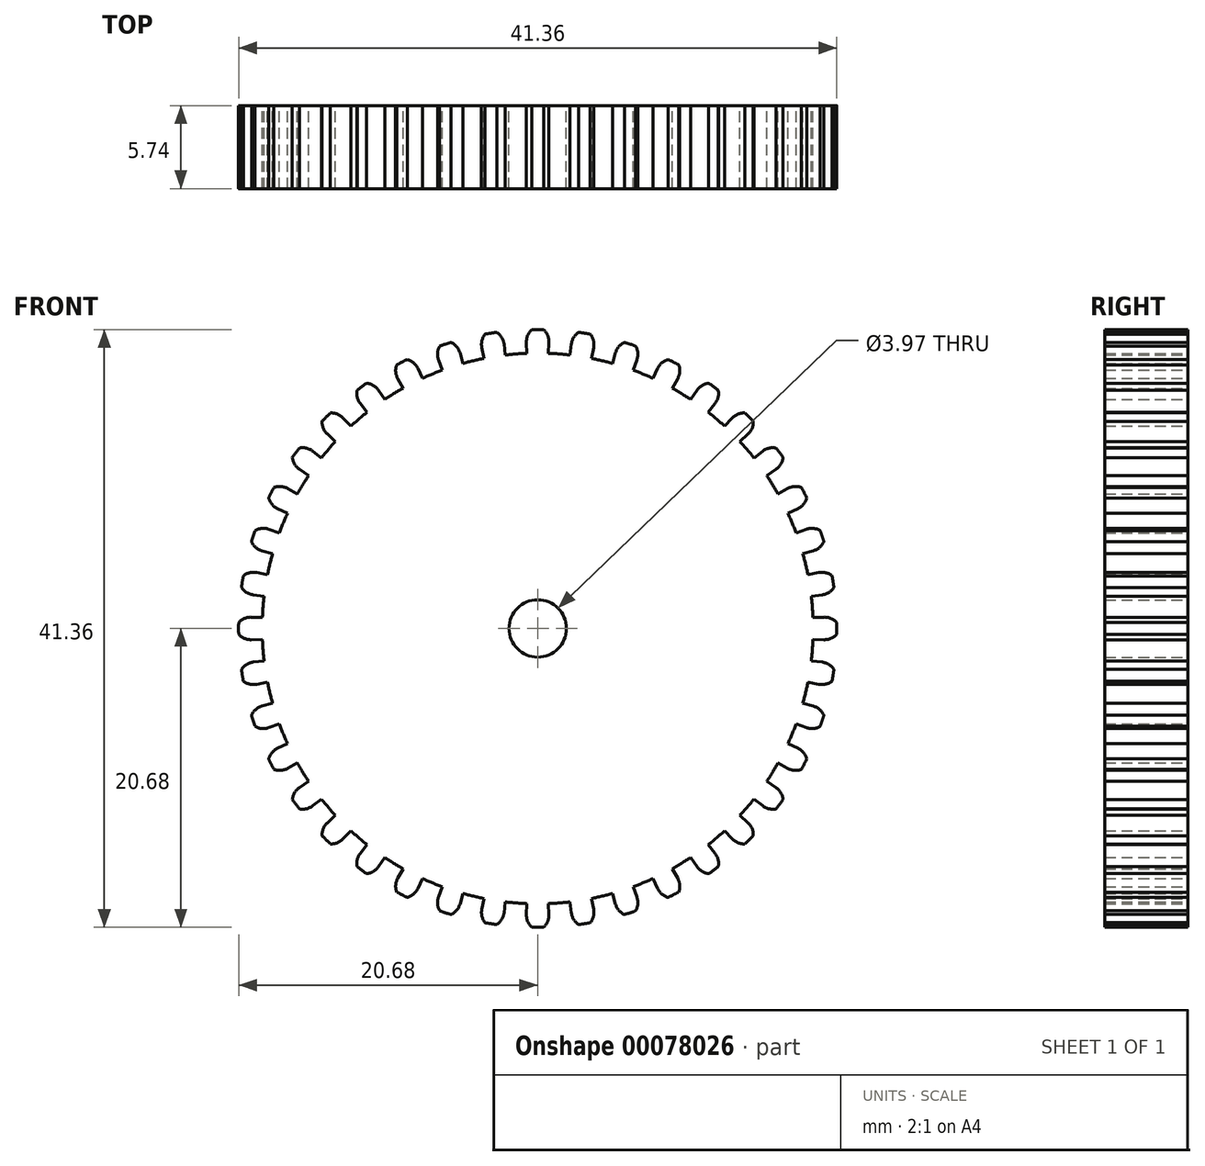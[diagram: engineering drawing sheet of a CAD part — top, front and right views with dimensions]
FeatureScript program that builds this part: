
annotation { "Feature Type Name" : "Feature", "Feature Type Description" : "" }
export const myFeature = defineFeature(function(context is Context, id is Id, definition is map)
    precondition{}
    {
        {
            var Q0;
            Q0=qCreatedBy(makeId("Front.planeOp"),FACE);
            var sketch = newSketch(context, id + "F0", { "sketchPlane" : qUnion([Q0])});
            skCircle(sketch, "E0", {"center": v(0, 0) * mm, "radius": 20.68 * mm, "construction": true});
            skCircle(sketch, "E1", {"center": v(0, 0) * mm, "radius": 19.81 * mm, "construction": true});
            skCircle(sketch, "E2", {"center": v(0, 0) * mm, "radius": 19.05 * mm, "construction": true});
            skLineSegment(sketch, "E3", {"start": v(0, 0) * mm, "end": v(19, 1.5) * mm, "construction": true});
            skLineSegment(sketch, "E4", {"start": v(0, 0) * mm, "end": v(6.61, 0) * mm, "construction": true});
            skLineSegment(sketch, "E5", {"start": v(0, 0) * mm, "end": v(6.8, 0.27) * mm, "construction": true});
            skLineSegment(sketch, "E6", {"start": v(0, 0) * mm, "end": v(7.15, 0.14) * mm, "construction": true});
            skArc(sketch, "E7", {"start": v(20.68, 0.4) * mm, "mid": v(20.68, 0.2) * mm, "end": v(20.68, 0) * mm});
            skArc(sketch, "E8", {"start": v(19, 1.5) * mm, "mid": v(19.02, 1.12) * mm, "end": v(19.04, 0.75) * mm});
            skLineSegment(sketch, "E9", {"start": v(19.04, 0.75) * mm, "end": v(19.8, 0.78) * mm});
            skArc(sketch, "E10", {"start": v(19.8, 0.78) * mm, "mid": v(20.28, 0.7) * mm, "end": v(20.68, 0.4) * mm});
            skLineSegment(sketch, "E11", {"start": v(0, 0) * mm, "end": v(19, 1.5) * mm});
            skLineSegment(sketch, "E12", {"start": v(0, 0) * mm, "end": v(20.68, 0) * mm});
            skArc(sketch, "E13.MirrorCS", {"start": v(19, -1.5) * mm, "mid": v(19.02, -1.12) * mm, "end": v(19.04, -0.75) * mm});
            skLineSegment(sketch, "E14.MirrorCS", {"start": v(19.04, -0.75) * mm, "end": v(19.8, -0.78) * mm});
            skArc(sketch, "E15.MirrorCS", {"start": v(19.8, -0.78) * mm, "mid": v(20.28, -0.7) * mm, "end": v(20.68, -0.4) * mm});
            skArc(sketch, "E16.MirrorCS", {"start": v(20.68, -0.4) * mm, "mid": v(20.68, -0.2) * mm, "end": v(20.68, 0) * mm});
            skArc(sketch, "E17.1.0", {"start": v(18.52, 4.45) * mm, "mid": v(18.6, 4.08) * mm, "end": v(18.68, 3.72) * mm});
            skLineSegment(sketch, "E17.1.1", {"start": v(18.68, 3.72) * mm, "end": v(19.43, 3.87) * mm});
            skArc(sketch, "E17.1.2", {"start": v(19.43, 3.87) * mm, "mid": v(19.92, 3.85) * mm, "end": v(20.36, 3.64) * mm});
            skArc(sketch, "E17.1.3", {"start": v(20.36, 3.64) * mm, "mid": v(20.4, 3.44) * mm, "end": v(20.43, 3.24) * mm});
            skArc(sketch, "E17.1.4", {"start": v(20.49, 2.83) * mm, "mid": v(20.46, 3.03) * mm, "end": v(20.43, 3.24) * mm});
            skArc(sketch, "E17.1.5", {"start": v(19.67, 2.33) * mm, "mid": v(20.14, 2.5) * mm, "end": v(20.49, 2.83) * mm});
            skLineSegment(sketch, "E17.1.6", {"start": v(18.92, 2.24) * mm, "end": v(19.67, 2.33) * mm});
            skArc(sketch, "E17.1.7", {"start": v(19, 1.5) * mm, "mid": v(18.96, 1.87) * mm, "end": v(18.92, 2.24) * mm});
            skArc(sketch, "E17.2.0", {"start": v(17.6, 7.3) * mm, "mid": v(17.74, 6.94) * mm, "end": v(17.87, 6.6) * mm});
            skLineSegment(sketch, "E17.2.1", {"start": v(17.87, 6.6) * mm, "end": v(18.59, 6.86) * mm});
            skArc(sketch, "E17.2.2", {"start": v(18.59, 6.86) * mm, "mid": v(19.07, 6.92) * mm, "end": v(19.54, 6.78) * mm});
            skArc(sketch, "E17.2.3", {"start": v(19.54, 6.78) * mm, "mid": v(19.6, 6.58) * mm, "end": v(19.67, 6.4) * mm});
            skArc(sketch, "E17.2.4", {"start": v(19.8, 6) * mm, "mid": v(19.73, 6.2) * mm, "end": v(19.67, 6.4) * mm});
            skArc(sketch, "E17.2.5", {"start": v(19.07, 5.38) * mm, "mid": v(19.5, 5.61) * mm, "end": v(19.8, 6) * mm});
            skLineSegment(sketch, "E17.2.6", {"start": v(18.33, 5.17) * mm, "end": v(19.07, 5.38) * mm});
            skArc(sketch, "E17.2.7", {"start": v(18.52, 4.45) * mm, "mid": v(18.43, 4.8) * mm, "end": v(18.33, 5.17) * mm});
            skArc(sketch, "E17.3.0", {"start": v(16.24, 9.95) * mm, "mid": v(16.44, 9.63) * mm, "end": v(16.62, 9.3) * mm});
            skLineSegment(sketch, "E17.3.1", {"start": v(16.62, 9.3) * mm, "end": v(17.29, 9.68) * mm});
            skArc(sketch, "E17.3.2", {"start": v(17.29, 9.68) * mm, "mid": v(17.76, 9.82) * mm, "end": v(18.24, 9.75) * mm});
            skArc(sketch, "E17.3.3", {"start": v(18.24, 9.75) * mm, "mid": v(18.33, 9.57) * mm, "end": v(18.43, 9.39) * mm});
            skArc(sketch, "E17.3.4", {"start": v(18.6, 9.03) * mm, "mid": v(18.52, 9.2) * mm, "end": v(18.43, 9.39) * mm});
            skArc(sketch, "E17.3.5", {"start": v(18, 8.3) * mm, "mid": v(18.38, 8.6) * mm, "end": v(18.6, 9.03) * mm});
            skLineSegment(sketch, "E17.3.6", {"start": v(17.3, 7.98) * mm, "end": v(18, 8.3) * mm});
            skArc(sketch, "E17.3.7", {"start": v(17.6, 7.3) * mm, "mid": v(17.45, 7.63) * mm, "end": v(17.3, 7.98) * mm});
            skArc(sketch, "E17.4.0", {"start": v(14.49, 12.37) * mm, "mid": v(14.73, 12.09) * mm, "end": v(14.96, 11.8) * mm});
            skLineSegment(sketch, "E17.4.1", {"start": v(14.96, 11.8) * mm, "end": v(15.56, 12.27) * mm});
            skArc(sketch, "E17.4.2", {"start": v(15.56, 12.27) * mm, "mid": v(16, 12.48) * mm, "end": v(16.5, 12.48) * mm});
            skArc(sketch, "E17.4.3", {"start": v(16.5, 12.48) * mm, "mid": v(16.61, 12.32) * mm, "end": v(16.73, 12.16) * mm});
            skArc(sketch, "E17.4.4", {"start": v(16.97, 11.83) * mm, "mid": v(16.85, 12) * mm, "end": v(16.73, 12.16) * mm});
            skArc(sketch, "E17.4.5", {"start": v(16.47, 11) * mm, "mid": v(16.81, 11.36) * mm, "end": v(16.97, 11.83) * mm});
            skLineSegment(sketch, "E17.4.6", {"start": v(15.84, 10.58) * mm, "end": v(16.47, 11) * mm});
            skArc(sketch, "E17.4.7", {"start": v(16.24, 9.95) * mm, "mid": v(16.04, 10.27) * mm, "end": v(15.84, 10.58) * mm});
            skArc(sketch, "E17.5.0", {"start": v(12.37, 14.49) * mm, "mid": v(12.65, 14.24) * mm, "end": v(12.93, 13.99) * mm});
            skLineSegment(sketch, "E17.5.1", {"start": v(12.93, 13.99) * mm, "end": v(13.45, 14.55) * mm});
            skArc(sketch, "E17.5.2", {"start": v(13.45, 14.55) * mm, "mid": v(13.85, 14.83) * mm, "end": v(14.33, 14.9) * mm});
            skArc(sketch, "E17.5.3", {"start": v(14.33, 14.9) * mm, "mid": v(14.48, 14.77) * mm, "end": v(14.62, 14.62) * mm});
            skArc(sketch, "E17.5.4", {"start": v(14.9, 14.33) * mm, "mid": v(14.77, 14.48) * mm, "end": v(14.62, 14.62) * mm});
            skArc(sketch, "E17.5.5", {"start": v(14.55, 13.45) * mm, "mid": v(14.83, 13.85) * mm, "end": v(14.9, 14.33) * mm});
            skLineSegment(sketch, "E17.5.6", {"start": v(13.99, 12.93) * mm, "end": v(14.55, 13.45) * mm});
            skArc(sketch, "E17.5.7", {"start": v(14.49, 12.37) * mm, "mid": v(14.24, 12.65) * mm, "end": v(13.99, 12.93) * mm});
            skArc(sketch, "E17.6.0", {"start": v(9.95, 16.24) * mm, "mid": v(10.27, 16.04) * mm, "end": v(10.58, 15.84) * mm});
            skLineSegment(sketch, "E17.6.1", {"start": v(10.58, 15.84) * mm, "end": v(11, 16.47) * mm});
            skArc(sketch, "E17.6.2", {"start": v(11, 16.47) * mm, "mid": v(11.36, 16.81) * mm, "end": v(11.83, 16.97) * mm});
            skArc(sketch, "E17.6.3", {"start": v(11.83, 16.97) * mm, "mid": v(12, 16.85) * mm, "end": v(12.16, 16.73) * mm});
            skArc(sketch, "E17.6.4", {"start": v(12.48, 16.5) * mm, "mid": v(12.32, 16.61) * mm, "end": v(12.16, 16.73) * mm});
            skArc(sketch, "E17.6.5", {"start": v(12.27, 15.56) * mm, "mid": v(12.48, 16) * mm, "end": v(12.48, 16.5) * mm});
            skLineSegment(sketch, "E17.6.6", {"start": v(11.8, 14.96) * mm, "end": v(12.27, 15.56) * mm});
            skArc(sketch, "E17.6.7", {"start": v(12.37, 14.49) * mm, "mid": v(12.09, 14.73) * mm, "end": v(11.8, 14.96) * mm});
            skArc(sketch, "E17.7.0", {"start": v(7.3, 17.6) * mm, "mid": v(7.63, 17.45) * mm, "end": v(7.98, 17.3) * mm});
            skLineSegment(sketch, "E17.7.1", {"start": v(7.98, 17.3) * mm, "end": v(8.3, 18) * mm});
            skArc(sketch, "E17.7.2", {"start": v(8.3, 18) * mm, "mid": v(8.6, 18.38) * mm, "end": v(9.03, 18.6) * mm});
            skArc(sketch, "E17.7.3", {"start": v(9.03, 18.6) * mm, "mid": v(9.2, 18.52) * mm, "end": v(9.39, 18.43) * mm});
            skArc(sketch, "E17.7.4", {"start": v(9.75, 18.24) * mm, "mid": v(9.57, 18.33) * mm, "end": v(9.39, 18.43) * mm});
            skArc(sketch, "E17.7.5", {"start": v(9.68, 17.29) * mm, "mid": v(9.82, 17.76) * mm, "end": v(9.75, 18.24) * mm});
            skLineSegment(sketch, "E17.7.6", {"start": v(9.3, 16.62) * mm, "end": v(9.68, 17.29) * mm});
            skArc(sketch, "E17.7.7", {"start": v(9.95, 16.24) * mm, "mid": v(9.63, 16.44) * mm, "end": v(9.3, 16.62) * mm});
            skArc(sketch, "E17.8.0", {"start": v(4.45, 18.52) * mm, "mid": v(4.8, 18.43) * mm, "end": v(5.17, 18.33) * mm});
            skLineSegment(sketch, "E17.8.1", {"start": v(5.17, 18.33) * mm, "end": v(5.38, 19.07) * mm});
            skArc(sketch, "E17.8.2", {"start": v(5.38, 19.07) * mm, "mid": v(5.61, 19.5) * mm, "end": v(6, 19.8) * mm});
            skArc(sketch, "E17.8.3", {"start": v(6, 19.8) * mm, "mid": v(6.2, 19.73) * mm, "end": v(6.4, 19.67) * mm});
            skArc(sketch, "E17.8.4", {"start": v(6.78, 19.54) * mm, "mid": v(6.58, 19.6) * mm, "end": v(6.4, 19.67) * mm});
            skArc(sketch, "E17.8.5", {"start": v(6.86, 18.59) * mm, "mid": v(6.92, 19.07) * mm, "end": v(6.78, 19.54) * mm});
            skLineSegment(sketch, "E17.8.6", {"start": v(6.6, 17.87) * mm, "end": v(6.86, 18.59) * mm});
            skArc(sketch, "E17.8.7", {"start": v(7.3, 17.6) * mm, "mid": v(6.94, 17.74) * mm, "end": v(6.6, 17.87) * mm});
            skArc(sketch, "E17.9.0", {"start": v(1.5, 19) * mm, "mid": v(1.87, 18.96) * mm, "end": v(2.24, 18.92) * mm});
            skLineSegment(sketch, "E17.9.1", {"start": v(2.24, 18.92) * mm, "end": v(2.33, 19.67) * mm});
            skArc(sketch, "E17.9.2", {"start": v(2.33, 19.67) * mm, "mid": v(2.5, 20.14) * mm, "end": v(2.83, 20.49) * mm});
            skArc(sketch, "E17.9.3", {"start": v(2.83, 20.49) * mm, "mid": v(3.03, 20.46) * mm, "end": v(3.24, 20.43) * mm});
            skArc(sketch, "E17.9.4", {"start": v(3.64, 20.36) * mm, "mid": v(3.44, 20.4) * mm, "end": v(3.24, 20.43) * mm});
            skArc(sketch, "E17.9.5", {"start": v(3.87, 19.43) * mm, "mid": v(3.85, 19.92) * mm, "end": v(3.64, 20.36) * mm});
            skLineSegment(sketch, "E17.9.6", {"start": v(3.72, 18.68) * mm, "end": v(3.87, 19.43) * mm});
            skArc(sketch, "E17.9.7", {"start": v(4.45, 18.52) * mm, "mid": v(4.08, 18.6) * mm, "end": v(3.72, 18.68) * mm});
            skCircle(sketch, "E18", {"center": v(0, 0) * mm, "radius": 1.98 * mm});
            skArc(sketch, "E19.1.10.0", {"start": v(-1.5, 19) * mm, "mid": v(-1.12, 19.02) * mm, "end": v(-0.75, 19.04) * mm});
            skLineSegment(sketch, "E19.4.10.0", {"start": v(-0.75, 19.04) * mm, "end": v(-0.78, 19.8) * mm});
            skArc(sketch, "E19.7.10.0", {"start": v(-0.78, 19.8) * mm, "mid": v(-0.7, 20.28) * mm, "end": v(-0.4, 20.68) * mm});
            skArc(sketch, "E19.11.10.0", {"start": v(-0.4, 20.68) * mm, "mid": v(-0.2, 20.68) * mm, "end": v(0, 20.68) * mm});
            skArc(sketch, "E19.15.10.0", {"start": v(0.4, 20.68) * mm, "mid": v(0.2, 20.68) * mm, "end": v(0, 20.68) * mm});
            skArc(sketch, "E19.19.10.0", {"start": v(0.78, 19.8) * mm, "mid": v(0.7, 20.28) * mm, "end": v(0.4, 20.68) * mm});
            skLineSegment(sketch, "E19.23.10.0", {"start": v(0.75, 19.04) * mm, "end": v(0.78, 19.8) * mm});
            skArc(sketch, "E19.26.10.0", {"start": v(1.5, 19) * mm, "mid": v(1.12, 19.02) * mm, "end": v(0.75, 19.04) * mm});
            skArc(sketch, "E19.1.11.0", {"start": v(-4.45, 18.52) * mm, "mid": v(-4.08, 18.6) * mm, "end": v(-3.72, 18.68) * mm});
            skLineSegment(sketch, "E19.4.11.0", {"start": v(-3.72, 18.68) * mm, "end": v(-3.87, 19.43) * mm});
            skArc(sketch, "E19.7.11.0", {"start": v(-3.87, 19.43) * mm, "mid": v(-3.85, 19.92) * mm, "end": v(-3.64, 20.36) * mm});
            skArc(sketch, "E19.11.11.0", {"start": v(-3.64, 20.36) * mm, "mid": v(-3.44, 20.4) * mm, "end": v(-3.24, 20.43) * mm});
            skArc(sketch, "E19.15.11.0", {"start": v(-2.83, 20.49) * mm, "mid": v(-3.03, 20.46) * mm, "end": v(-3.24, 20.43) * mm});
            skArc(sketch, "E19.19.11.0", {"start": v(-2.33, 19.67) * mm, "mid": v(-2.5, 20.14) * mm, "end": v(-2.83, 20.49) * mm});
            skLineSegment(sketch, "E19.23.11.0", {"start": v(-2.24, 18.92) * mm, "end": v(-2.33, 19.67) * mm});
            skArc(sketch, "E19.26.11.0", {"start": v(-1.5, 19) * mm, "mid": v(-1.87, 18.96) * mm, "end": v(-2.24, 18.92) * mm});
            skArc(sketch, "E19.1.12.0", {"start": v(-7.3, 17.6) * mm, "mid": v(-6.94, 17.74) * mm, "end": v(-6.6, 17.87) * mm});
            skLineSegment(sketch, "E19.4.12.0", {"start": v(-6.6, 17.87) * mm, "end": v(-6.86, 18.59) * mm});
            skArc(sketch, "E19.7.12.0", {"start": v(-6.86, 18.59) * mm, "mid": v(-6.92, 19.07) * mm, "end": v(-6.78, 19.54) * mm});
            skArc(sketch, "E19.11.12.0", {"start": v(-6.78, 19.54) * mm, "mid": v(-6.58, 19.6) * mm, "end": v(-6.4, 19.67) * mm});
            skArc(sketch, "E19.15.12.0", {"start": v(-6, 19.8) * mm, "mid": v(-6.2, 19.73) * mm, "end": v(-6.4, 19.67) * mm});
            skArc(sketch, "E19.19.12.0", {"start": v(-5.38, 19.07) * mm, "mid": v(-5.61, 19.5) * mm, "end": v(-6, 19.8) * mm});
            skLineSegment(sketch, "E19.23.12.0", {"start": v(-5.17, 18.33) * mm, "end": v(-5.38, 19.07) * mm});
            skArc(sketch, "E19.26.12.0", {"start": v(-4.45, 18.52) * mm, "mid": v(-4.8, 18.43) * mm, "end": v(-5.17, 18.33) * mm});
            skArc(sketch, "E19.1.13.0", {"start": v(-9.95, 16.24) * mm, "mid": v(-9.63, 16.44) * mm, "end": v(-9.3, 16.62) * mm});
            skLineSegment(sketch, "E19.4.13.0", {"start": v(-9.3, 16.62) * mm, "end": v(-9.68, 17.29) * mm});
            skArc(sketch, "E19.7.13.0", {"start": v(-9.68, 17.29) * mm, "mid": v(-9.82, 17.76) * mm, "end": v(-9.75, 18.24) * mm});
            skArc(sketch, "E19.11.13.0", {"start": v(-9.75, 18.24) * mm, "mid": v(-9.57, 18.33) * mm, "end": v(-9.39, 18.43) * mm});
            skArc(sketch, "E19.15.13.0", {"start": v(-9.03, 18.6) * mm, "mid": v(-9.2, 18.52) * mm, "end": v(-9.39, 18.43) * mm});
            skArc(sketch, "E19.19.13.0", {"start": v(-8.3, 18) * mm, "mid": v(-8.6, 18.38) * mm, "end": v(-9.03, 18.6) * mm});
            skLineSegment(sketch, "E19.23.13.0", {"start": v(-7.98, 17.3) * mm, "end": v(-8.3, 18) * mm});
            skArc(sketch, "E19.26.13.0", {"start": v(-7.3, 17.6) * mm, "mid": v(-7.63, 17.45) * mm, "end": v(-7.98, 17.3) * mm});
            skArc(sketch, "E19.1.14.0", {"start": v(-12.37, 14.49) * mm, "mid": v(-12.09, 14.73) * mm, "end": v(-11.8, 14.96) * mm});
            skLineSegment(sketch, "E19.4.14.0", {"start": v(-11.8, 14.96) * mm, "end": v(-12.27, 15.56) * mm});
            skArc(sketch, "E19.7.14.0", {"start": v(-12.27, 15.56) * mm, "mid": v(-12.48, 16) * mm, "end": v(-12.48, 16.5) * mm});
            skArc(sketch, "E19.11.14.0", {"start": v(-12.48, 16.5) * mm, "mid": v(-12.32, 16.61) * mm, "end": v(-12.16, 16.73) * mm});
            skArc(sketch, "E19.15.14.0", {"start": v(-11.83, 16.97) * mm, "mid": v(-12, 16.85) * mm, "end": v(-12.16, 16.73) * mm});
            skArc(sketch, "E19.19.14.0", {"start": v(-11, 16.47) * mm, "mid": v(-11.36, 16.81) * mm, "end": v(-11.83, 16.97) * mm});
            skLineSegment(sketch, "E19.23.14.0", {"start": v(-10.58, 15.84) * mm, "end": v(-11, 16.47) * mm});
            skArc(sketch, "E19.26.14.0", {"start": v(-9.95, 16.24) * mm, "mid": v(-10.27, 16.04) * mm, "end": v(-10.58, 15.84) * mm});
            skArc(sketch, "E19.1.15.0", {"start": v(-14.49, 12.37) * mm, "mid": v(-14.24, 12.65) * mm, "end": v(-13.99, 12.93) * mm});
            skLineSegment(sketch, "E19.4.15.0", {"start": v(-13.99, 12.93) * mm, "end": v(-14.55, 13.45) * mm});
            skArc(sketch, "E19.7.15.0", {"start": v(-14.55, 13.45) * mm, "mid": v(-14.83, 13.85) * mm, "end": v(-14.9, 14.33) * mm});
            skArc(sketch, "E19.11.15.0", {"start": v(-14.9, 14.33) * mm, "mid": v(-14.77, 14.48) * mm, "end": v(-14.62, 14.62) * mm});
            skArc(sketch, "E19.15.15.0", {"start": v(-14.33, 14.9) * mm, "mid": v(-14.48, 14.77) * mm, "end": v(-14.62, 14.62) * mm});
            skArc(sketch, "E19.19.15.0", {"start": v(-13.45, 14.55) * mm, "mid": v(-13.85, 14.83) * mm, "end": v(-14.33, 14.9) * mm});
            skLineSegment(sketch, "E19.23.15.0", {"start": v(-12.93, 13.99) * mm, "end": v(-13.45, 14.55) * mm});
            skArc(sketch, "E19.26.15.0", {"start": v(-12.37, 14.49) * mm, "mid": v(-12.65, 14.24) * mm, "end": v(-12.93, 13.99) * mm});
            skArc(sketch, "E19.1.16.0", {"start": v(-16.24, 9.95) * mm, "mid": v(-16.04, 10.27) * mm, "end": v(-15.84, 10.58) * mm});
            skLineSegment(sketch, "E19.4.16.0", {"start": v(-15.84, 10.58) * mm, "end": v(-16.47, 11) * mm});
            skArc(sketch, "E19.7.16.0", {"start": v(-16.47, 11) * mm, "mid": v(-16.81, 11.36) * mm, "end": v(-16.97, 11.83) * mm});
            skArc(sketch, "E19.11.16.0", {"start": v(-16.97, 11.83) * mm, "mid": v(-16.85, 12) * mm, "end": v(-16.73, 12.16) * mm});
            skArc(sketch, "E19.15.16.0", {"start": v(-16.5, 12.48) * mm, "mid": v(-16.61, 12.32) * mm, "end": v(-16.73, 12.16) * mm});
            skArc(sketch, "E19.19.16.0", {"start": v(-15.56, 12.27) * mm, "mid": v(-16, 12.48) * mm, "end": v(-16.5, 12.48) * mm});
            skLineSegment(sketch, "E19.23.16.0", {"start": v(-14.96, 11.8) * mm, "end": v(-15.56, 12.27) * mm});
            skArc(sketch, "E19.26.16.0", {"start": v(-14.49, 12.37) * mm, "mid": v(-14.73, 12.09) * mm, "end": v(-14.96, 11.8) * mm});
            skArc(sketch, "E19.1.17.0", {"start": v(-17.6, 7.3) * mm, "mid": v(-17.45, 7.63) * mm, "end": v(-17.3, 7.98) * mm});
            skLineSegment(sketch, "E19.4.17.0", {"start": v(-17.3, 7.98) * mm, "end": v(-18, 8.3) * mm});
            skArc(sketch, "E19.7.17.0", {"start": v(-18, 8.3) * mm, "mid": v(-18.38, 8.6) * mm, "end": v(-18.6, 9.03) * mm});
            skArc(sketch, "E19.11.17.0", {"start": v(-18.6, 9.03) * mm, "mid": v(-18.52, 9.2) * mm, "end": v(-18.43, 9.39) * mm});
            skArc(sketch, "E19.15.17.0", {"start": v(-18.24, 9.75) * mm, "mid": v(-18.33, 9.57) * mm, "end": v(-18.43, 9.39) * mm});
            skArc(sketch, "E19.19.17.0", {"start": v(-17.29, 9.68) * mm, "mid": v(-17.76, 9.82) * mm, "end": v(-18.24, 9.75) * mm});
            skLineSegment(sketch, "E19.23.17.0", {"start": v(-16.62, 9.3) * mm, "end": v(-17.29, 9.68) * mm});
            skArc(sketch, "E19.26.17.0", {"start": v(-16.24, 9.95) * mm, "mid": v(-16.44, 9.63) * mm, "end": v(-16.62, 9.3) * mm});
            skArc(sketch, "E19.1.18.0", {"start": v(-18.52, 4.45) * mm, "mid": v(-18.43, 4.8) * mm, "end": v(-18.33, 5.17) * mm});
            skLineSegment(sketch, "E19.4.18.0", {"start": v(-18.33, 5.17) * mm, "end": v(-19.07, 5.38) * mm});
            skArc(sketch, "E19.7.18.0", {"start": v(-19.07, 5.38) * mm, "mid": v(-19.5, 5.61) * mm, "end": v(-19.8, 6) * mm});
            skArc(sketch, "E19.11.18.0", {"start": v(-19.8, 6) * mm, "mid": v(-19.73, 6.2) * mm, "end": v(-19.67, 6.4) * mm});
            skArc(sketch, "E19.15.18.0", {"start": v(-19.54, 6.78) * mm, "mid": v(-19.6, 6.58) * mm, "end": v(-19.67, 6.4) * mm});
            skArc(sketch, "E19.19.18.0", {"start": v(-18.59, 6.86) * mm, "mid": v(-19.07, 6.92) * mm, "end": v(-19.54, 6.78) * mm});
            skLineSegment(sketch, "E19.23.18.0", {"start": v(-17.87, 6.6) * mm, "end": v(-18.59, 6.86) * mm});
            skArc(sketch, "E19.26.18.0", {"start": v(-17.6, 7.3) * mm, "mid": v(-17.74, 6.94) * mm, "end": v(-17.87, 6.6) * mm});
            skArc(sketch, "E19.1.19.0", {"start": v(-19, 1.5) * mm, "mid": v(-18.96, 1.87) * mm, "end": v(-18.92, 2.24) * mm});
            skLineSegment(sketch, "E19.4.19.0", {"start": v(-18.92, 2.24) * mm, "end": v(-19.67, 2.33) * mm});
            skArc(sketch, "E19.7.19.0", {"start": v(-19.67, 2.33) * mm, "mid": v(-20.14, 2.5) * mm, "end": v(-20.49, 2.83) * mm});
            skArc(sketch, "E19.11.19.0", {"start": v(-20.49, 2.83) * mm, "mid": v(-20.46, 3.03) * mm, "end": v(-20.43, 3.24) * mm});
            skArc(sketch, "E19.15.19.0", {"start": v(-20.36, 3.64) * mm, "mid": v(-20.4, 3.44) * mm, "end": v(-20.43, 3.24) * mm});
            skArc(sketch, "E19.19.19.0", {"start": v(-19.43, 3.87) * mm, "mid": v(-19.92, 3.85) * mm, "end": v(-20.36, 3.64) * mm});
            skLineSegment(sketch, "E19.23.19.0", {"start": v(-18.68, 3.72) * mm, "end": v(-19.43, 3.87) * mm});
            skArc(sketch, "E19.26.19.0", {"start": v(-18.52, 4.45) * mm, "mid": v(-18.6, 4.08) * mm, "end": v(-18.68, 3.72) * mm});
            skArc(sketch, "E19.1.20.0", {"start": v(-19, -1.5) * mm, "mid": v(-19.02, -1.12) * mm, "end": v(-19.04, -0.75) * mm});
            skLineSegment(sketch, "E19.4.20.0", {"start": v(-19.04, -0.75) * mm, "end": v(-19.8, -0.78) * mm});
            skArc(sketch, "E19.7.20.0", {"start": v(-19.8, -0.78) * mm, "mid": v(-20.28, -0.7) * mm, "end": v(-20.68, -0.4) * mm});
            skArc(sketch, "E19.11.20.0", {"start": v(-20.68, -0.4) * mm, "mid": v(-20.68, -0.2) * mm, "end": v(-20.68, 0) * mm});
            skArc(sketch, "E19.15.20.0", {"start": v(-20.68, 0.4) * mm, "mid": v(-20.68, 0.2) * mm, "end": v(-20.68, 0) * mm});
            skArc(sketch, "E19.19.20.0", {"start": v(-19.8, 0.78) * mm, "mid": v(-20.28, 0.7) * mm, "end": v(-20.68, 0.4) * mm});
            skLineSegment(sketch, "E19.23.20.0", {"start": v(-19.04, 0.75) * mm, "end": v(-19.8, 0.78) * mm});
            skArc(sketch, "E19.26.20.0", {"start": v(-19, 1.5) * mm, "mid": v(-19.02, 1.12) * mm, "end": v(-19.04, 0.75) * mm});
            skArc(sketch, "E19.1.21.0", {"start": v(-18.52, -4.45) * mm, "mid": v(-18.6, -4.08) * mm, "end": v(-18.68, -3.72) * mm});
            skLineSegment(sketch, "E19.4.21.0", {"start": v(-18.68, -3.72) * mm, "end": v(-19.43, -3.87) * mm});
            skArc(sketch, "E19.7.21.0", {"start": v(-19.43, -3.87) * mm, "mid": v(-19.92, -3.85) * mm, "end": v(-20.36, -3.64) * mm});
            skArc(sketch, "E19.11.21.0", {"start": v(-20.36, -3.64) * mm, "mid": v(-20.4, -3.44) * mm, "end": v(-20.43, -3.24) * mm});
            skArc(sketch, "E19.15.21.0", {"start": v(-20.49, -2.83) * mm, "mid": v(-20.46, -3.03) * mm, "end": v(-20.43, -3.24) * mm});
            skArc(sketch, "E19.19.21.0", {"start": v(-19.67, -2.33) * mm, "mid": v(-20.14, -2.5) * mm, "end": v(-20.49, -2.83) * mm});
            skLineSegment(sketch, "E19.23.21.0", {"start": v(-18.92, -2.24) * mm, "end": v(-19.67, -2.33) * mm});
            skArc(sketch, "E19.26.21.0", {"start": v(-19, -1.5) * mm, "mid": v(-18.96, -1.87) * mm, "end": v(-18.92, -2.24) * mm});
            skArc(sketch, "E19.1.22.0", {"start": v(-17.6, -7.3) * mm, "mid": v(-17.74, -6.94) * mm, "end": v(-17.87, -6.6) * mm});
            skLineSegment(sketch, "E19.4.22.0", {"start": v(-17.87, -6.6) * mm, "end": v(-18.59, -6.86) * mm});
            skArc(sketch, "E19.7.22.0", {"start": v(-18.59, -6.86) * mm, "mid": v(-19.07, -6.92) * mm, "end": v(-19.54, -6.78) * mm});
            skArc(sketch, "E19.11.22.0", {"start": v(-19.54, -6.78) * mm, "mid": v(-19.6, -6.58) * mm, "end": v(-19.67, -6.4) * mm});
            skArc(sketch, "E19.15.22.0", {"start": v(-19.8, -6) * mm, "mid": v(-19.73, -6.2) * mm, "end": v(-19.67, -6.4) * mm});
            skArc(sketch, "E19.19.22.0", {"start": v(-19.07, -5.38) * mm, "mid": v(-19.5, -5.61) * mm, "end": v(-19.8, -6) * mm});
            skLineSegment(sketch, "E19.23.22.0", {"start": v(-18.33, -5.17) * mm, "end": v(-19.07, -5.38) * mm});
            skArc(sketch, "E19.26.22.0", {"start": v(-18.52, -4.45) * mm, "mid": v(-18.43, -4.8) * mm, "end": v(-18.33, -5.17) * mm});
            skArc(sketch, "E19.1.23.0", {"start": v(-16.24, -9.95) * mm, "mid": v(-16.44, -9.63) * mm, "end": v(-16.62, -9.3) * mm});
            skLineSegment(sketch, "E19.4.23.0", {"start": v(-16.62, -9.3) * mm, "end": v(-17.29, -9.68) * mm});
            skArc(sketch, "E19.7.23.0", {"start": v(-17.29, -9.68) * mm, "mid": v(-17.76, -9.82) * mm, "end": v(-18.24, -9.75) * mm});
            skArc(sketch, "E19.11.23.0", {"start": v(-18.24, -9.75) * mm, "mid": v(-18.33, -9.57) * mm, "end": v(-18.43, -9.39) * mm});
            skArc(sketch, "E19.15.23.0", {"start": v(-18.6, -9.03) * mm, "mid": v(-18.52, -9.2) * mm, "end": v(-18.43, -9.39) * mm});
            skArc(sketch, "E19.19.23.0", {"start": v(-18, -8.3) * mm, "mid": v(-18.38, -8.6) * mm, "end": v(-18.6, -9.03) * mm});
            skLineSegment(sketch, "E19.23.23.0", {"start": v(-17.3, -7.98) * mm, "end": v(-18, -8.3) * mm});
            skArc(sketch, "E19.26.23.0", {"start": v(-17.6, -7.3) * mm, "mid": v(-17.45, -7.63) * mm, "end": v(-17.3, -7.98) * mm});
            skArc(sketch, "E19.1.24.0", {"start": v(-14.49, -12.37) * mm, "mid": v(-14.73, -12.09) * mm, "end": v(-14.96, -11.8) * mm});
            skLineSegment(sketch, "E19.4.24.0", {"start": v(-14.96, -11.8) * mm, "end": v(-15.56, -12.27) * mm});
            skArc(sketch, "E19.7.24.0", {"start": v(-15.56, -12.27) * mm, "mid": v(-16, -12.48) * mm, "end": v(-16.5, -12.48) * mm});
            skArc(sketch, "E19.11.24.0", {"start": v(-16.5, -12.48) * mm, "mid": v(-16.61, -12.32) * mm, "end": v(-16.73, -12.16) * mm});
            skArc(sketch, "E19.15.24.0", {"start": v(-16.97, -11.83) * mm, "mid": v(-16.85, -12) * mm, "end": v(-16.73, -12.16) * mm});
            skArc(sketch, "E19.19.24.0", {"start": v(-16.47, -11) * mm, "mid": v(-16.81, -11.36) * mm, "end": v(-16.97, -11.83) * mm});
            skLineSegment(sketch, "E19.23.24.0", {"start": v(-15.84, -10.58) * mm, "end": v(-16.47, -11) * mm});
            skArc(sketch, "E19.26.24.0", {"start": v(-16.24, -9.95) * mm, "mid": v(-16.04, -10.27) * mm, "end": v(-15.84, -10.58) * mm});
            skArc(sketch, "E19.1.25.0", {"start": v(-12.37, -14.49) * mm, "mid": v(-12.65, -14.24) * mm, "end": v(-12.93, -13.99) * mm});
            skLineSegment(sketch, "E19.4.25.0", {"start": v(-12.93, -13.99) * mm, "end": v(-13.45, -14.55) * mm});
            skArc(sketch, "E19.7.25.0", {"start": v(-13.45, -14.55) * mm, "mid": v(-13.85, -14.83) * mm, "end": v(-14.33, -14.9) * mm});
            skArc(sketch, "E19.11.25.0", {"start": v(-14.33, -14.9) * mm, "mid": v(-14.48, -14.77) * mm, "end": v(-14.62, -14.62) * mm});
            skArc(sketch, "E19.15.25.0", {"start": v(-14.9, -14.33) * mm, "mid": v(-14.77, -14.48) * mm, "end": v(-14.62, -14.62) * mm});
            skArc(sketch, "E19.19.25.0", {"start": v(-14.55, -13.45) * mm, "mid": v(-14.83, -13.85) * mm, "end": v(-14.9, -14.33) * mm});
            skLineSegment(sketch, "E19.23.25.0", {"start": v(-13.99, -12.93) * mm, "end": v(-14.55, -13.45) * mm});
            skArc(sketch, "E19.26.25.0", {"start": v(-14.49, -12.37) * mm, "mid": v(-14.24, -12.65) * mm, "end": v(-13.99, -12.93) * mm});
            skArc(sketch, "E19.1.26.0", {"start": v(-9.95, -16.24) * mm, "mid": v(-10.27, -16.04) * mm, "end": v(-10.58, -15.84) * mm});
            skLineSegment(sketch, "E19.4.26.0", {"start": v(-10.58, -15.84) * mm, "end": v(-11, -16.47) * mm});
            skArc(sketch, "E19.7.26.0", {"start": v(-11, -16.47) * mm, "mid": v(-11.36, -16.81) * mm, "end": v(-11.83, -16.97) * mm});
            skArc(sketch, "E19.11.26.0", {"start": v(-11.83, -16.97) * mm, "mid": v(-12, -16.85) * mm, "end": v(-12.16, -16.73) * mm});
            skArc(sketch, "E19.15.26.0", {"start": v(-12.48, -16.5) * mm, "mid": v(-12.32, -16.61) * mm, "end": v(-12.16, -16.73) * mm});
            skArc(sketch, "E19.19.26.0", {"start": v(-12.27, -15.56) * mm, "mid": v(-12.48, -16) * mm, "end": v(-12.48, -16.5) * mm});
            skLineSegment(sketch, "E19.23.26.0", {"start": v(-11.8, -14.96) * mm, "end": v(-12.27, -15.56) * mm});
            skArc(sketch, "E19.26.26.0", {"start": v(-12.37, -14.49) * mm, "mid": v(-12.09, -14.73) * mm, "end": v(-11.8, -14.96) * mm});
            skArc(sketch, "E19.1.27.0", {"start": v(-7.3, -17.6) * mm, "mid": v(-7.63, -17.45) * mm, "end": v(-7.98, -17.3) * mm});
            skLineSegment(sketch, "E19.4.27.0", {"start": v(-7.98, -17.3) * mm, "end": v(-8.3, -18) * mm});
            skArc(sketch, "E19.7.27.0", {"start": v(-8.3, -18) * mm, "mid": v(-8.6, -18.38) * mm, "end": v(-9.03, -18.6) * mm});
            skArc(sketch, "E19.11.27.0", {"start": v(-9.03, -18.6) * mm, "mid": v(-9.2, -18.52) * mm, "end": v(-9.39, -18.43) * mm});
            skArc(sketch, "E19.15.27.0", {"start": v(-9.75, -18.24) * mm, "mid": v(-9.57, -18.33) * mm, "end": v(-9.39, -18.43) * mm});
            skArc(sketch, "E19.19.27.0", {"start": v(-9.68, -17.29) * mm, "mid": v(-9.82, -17.76) * mm, "end": v(-9.75, -18.24) * mm});
            skLineSegment(sketch, "E19.23.27.0", {"start": v(-9.3, -16.62) * mm, "end": v(-9.68, -17.29) * mm});
            skArc(sketch, "E19.26.27.0", {"start": v(-9.95, -16.24) * mm, "mid": v(-9.63, -16.44) * mm, "end": v(-9.3, -16.62) * mm});
            skArc(sketch, "E19.1.28.0", {"start": v(-4.45, -18.52) * mm, "mid": v(-4.8, -18.43) * mm, "end": v(-5.17, -18.33) * mm});
            skLineSegment(sketch, "E19.4.28.0", {"start": v(-5.17, -18.33) * mm, "end": v(-5.38, -19.07) * mm});
            skArc(sketch, "E19.7.28.0", {"start": v(-5.38, -19.07) * mm, "mid": v(-5.61, -19.5) * mm, "end": v(-6, -19.8) * mm});
            skArc(sketch, "E19.11.28.0", {"start": v(-6, -19.8) * mm, "mid": v(-6.2, -19.73) * mm, "end": v(-6.4, -19.67) * mm});
            skArc(sketch, "E19.15.28.0", {"start": v(-6.78, -19.54) * mm, "mid": v(-6.58, -19.6) * mm, "end": v(-6.4, -19.67) * mm});
            skArc(sketch, "E19.19.28.0", {"start": v(-6.86, -18.59) * mm, "mid": v(-6.92, -19.07) * mm, "end": v(-6.78, -19.54) * mm});
            skLineSegment(sketch, "E19.23.28.0", {"start": v(-6.6, -17.87) * mm, "end": v(-6.86, -18.59) * mm});
            skArc(sketch, "E19.26.28.0", {"start": v(-7.3, -17.6) * mm, "mid": v(-6.94, -17.74) * mm, "end": v(-6.6, -17.87) * mm});
            skArc(sketch, "E19.1.29.0", {"start": v(-1.5, -19) * mm, "mid": v(-1.87, -18.96) * mm, "end": v(-2.24, -18.92) * mm});
            skLineSegment(sketch, "E19.4.29.0", {"start": v(-2.24, -18.92) * mm, "end": v(-2.33, -19.67) * mm});
            skArc(sketch, "E19.7.29.0", {"start": v(-2.33, -19.67) * mm, "mid": v(-2.5, -20.14) * mm, "end": v(-2.83, -20.49) * mm});
            skArc(sketch, "E19.11.29.0", {"start": v(-2.83, -20.49) * mm, "mid": v(-3.03, -20.46) * mm, "end": v(-3.24, -20.43) * mm});
            skArc(sketch, "E19.15.29.0", {"start": v(-3.64, -20.36) * mm, "mid": v(-3.44, -20.4) * mm, "end": v(-3.24, -20.43) * mm});
            skArc(sketch, "E19.19.29.0", {"start": v(-3.87, -19.43) * mm, "mid": v(-3.85, -19.92) * mm, "end": v(-3.64, -20.36) * mm});
            skLineSegment(sketch, "E19.23.29.0", {"start": v(-3.72, -18.68) * mm, "end": v(-3.87, -19.43) * mm});
            skArc(sketch, "E19.26.29.0", {"start": v(-4.45, -18.52) * mm, "mid": v(-4.08, -18.6) * mm, "end": v(-3.72, -18.68) * mm});
            skArc(sketch, "E19.1.30.0", {"start": v(1.5, -19) * mm, "mid": v(1.12, -19.02) * mm, "end": v(0.75, -19.04) * mm});
            skLineSegment(sketch, "E19.4.30.0", {"start": v(0.75, -19.04) * mm, "end": v(0.78, -19.8) * mm});
            skArc(sketch, "E19.7.30.0", {"start": v(0.78, -19.8) * mm, "mid": v(0.7, -20.28) * mm, "end": v(0.4, -20.68) * mm});
            skArc(sketch, "E19.11.30.0", {"start": v(0.4, -20.68) * mm, "mid": v(0.2, -20.68) * mm, "end": v(0, -20.68) * mm});
            skArc(sketch, "E19.15.30.0", {"start": v(-0.4, -20.68) * mm, "mid": v(-0.2, -20.68) * mm, "end": v(0, -20.68) * mm});
            skArc(sketch, "E19.19.30.0", {"start": v(-0.78, -19.8) * mm, "mid": v(-0.7, -20.28) * mm, "end": v(-0.4, -20.68) * mm});
            skLineSegment(sketch, "E19.23.30.0", {"start": v(-0.75, -19.04) * mm, "end": v(-0.78, -19.8) * mm});
            skArc(sketch, "E19.26.30.0", {"start": v(-1.5, -19) * mm, "mid": v(-1.12, -19.02) * mm, "end": v(-0.75, -19.04) * mm});
            skArc(sketch, "E19.1.31.0", {"start": v(4.45, -18.52) * mm, "mid": v(4.08, -18.6) * mm, "end": v(3.72, -18.68) * mm});
            skLineSegment(sketch, "E19.4.31.0", {"start": v(3.72, -18.68) * mm, "end": v(3.87, -19.43) * mm});
            skArc(sketch, "E19.7.31.0", {"start": v(3.87, -19.43) * mm, "mid": v(3.85, -19.92) * mm, "end": v(3.64, -20.36) * mm});
            skArc(sketch, "E19.11.31.0", {"start": v(3.64, -20.36) * mm, "mid": v(3.44, -20.4) * mm, "end": v(3.24, -20.43) * mm});
            skArc(sketch, "E19.15.31.0", {"start": v(2.83, -20.49) * mm, "mid": v(3.03, -20.46) * mm, "end": v(3.24, -20.43) * mm});
            skArc(sketch, "E19.19.31.0", {"start": v(2.33, -19.67) * mm, "mid": v(2.5, -20.14) * mm, "end": v(2.83, -20.49) * mm});
            skLineSegment(sketch, "E19.23.31.0", {"start": v(2.24, -18.92) * mm, "end": v(2.33, -19.67) * mm});
            skArc(sketch, "E19.26.31.0", {"start": v(1.5, -19) * mm, "mid": v(1.87, -18.96) * mm, "end": v(2.24, -18.92) * mm});
            skArc(sketch, "E19.1.32.0", {"start": v(7.3, -17.6) * mm, "mid": v(6.94, -17.74) * mm, "end": v(6.6, -17.87) * mm});
            skLineSegment(sketch, "E19.4.32.0", {"start": v(6.6, -17.87) * mm, "end": v(6.86, -18.59) * mm});
            skArc(sketch, "E19.7.32.0", {"start": v(6.86, -18.59) * mm, "mid": v(6.92, -19.07) * mm, "end": v(6.78, -19.54) * mm});
            skArc(sketch, "E19.11.32.0", {"start": v(6.78, -19.54) * mm, "mid": v(6.58, -19.6) * mm, "end": v(6.4, -19.67) * mm});
            skArc(sketch, "E19.15.32.0", {"start": v(6, -19.8) * mm, "mid": v(6.2, -19.73) * mm, "end": v(6.4, -19.67) * mm});
            skArc(sketch, "E19.19.32.0", {"start": v(5.38, -19.07) * mm, "mid": v(5.61, -19.5) * mm, "end": v(6, -19.8) * mm});
            skLineSegment(sketch, "E19.23.32.0", {"start": v(5.17, -18.33) * mm, "end": v(5.38, -19.07) * mm});
            skArc(sketch, "E19.26.32.0", {"start": v(4.45, -18.52) * mm, "mid": v(4.8, -18.43) * mm, "end": v(5.17, -18.33) * mm});
            skArc(sketch, "E19.1.33.0", {"start": v(9.95, -16.24) * mm, "mid": v(9.63, -16.44) * mm, "end": v(9.3, -16.62) * mm});
            skLineSegment(sketch, "E19.4.33.0", {"start": v(9.3, -16.62) * mm, "end": v(9.68, -17.29) * mm});
            skArc(sketch, "E19.7.33.0", {"start": v(9.68, -17.29) * mm, "mid": v(9.82, -17.76) * mm, "end": v(9.75, -18.24) * mm});
            skArc(sketch, "E19.11.33.0", {"start": v(9.75, -18.24) * mm, "mid": v(9.57, -18.33) * mm, "end": v(9.39, -18.43) * mm});
            skArc(sketch, "E19.15.33.0", {"start": v(9.03, -18.6) * mm, "mid": v(9.2, -18.52) * mm, "end": v(9.39, -18.43) * mm});
            skArc(sketch, "E19.19.33.0", {"start": v(8.3, -18) * mm, "mid": v(8.6, -18.38) * mm, "end": v(9.03, -18.6) * mm});
            skLineSegment(sketch, "E19.23.33.0", {"start": v(7.98, -17.3) * mm, "end": v(8.3, -18) * mm});
            skArc(sketch, "E19.26.33.0", {"start": v(7.3, -17.6) * mm, "mid": v(7.63, -17.45) * mm, "end": v(7.98, -17.3) * mm});
            skArc(sketch, "E19.1.34.0", {"start": v(12.37, -14.49) * mm, "mid": v(12.09, -14.73) * mm, "end": v(11.8, -14.96) * mm});
            skLineSegment(sketch, "E19.4.34.0", {"start": v(11.8, -14.96) * mm, "end": v(12.27, -15.56) * mm});
            skArc(sketch, "E19.7.34.0", {"start": v(12.27, -15.56) * mm, "mid": v(12.48, -16) * mm, "end": v(12.48, -16.5) * mm});
            skArc(sketch, "E19.11.34.0", {"start": v(12.48, -16.5) * mm, "mid": v(12.32, -16.61) * mm, "end": v(12.16, -16.73) * mm});
            skArc(sketch, "E19.15.34.0", {"start": v(11.83, -16.97) * mm, "mid": v(12, -16.85) * mm, "end": v(12.16, -16.73) * mm});
            skArc(sketch, "E19.19.34.0", {"start": v(11, -16.47) * mm, "mid": v(11.36, -16.81) * mm, "end": v(11.83, -16.97) * mm});
            skLineSegment(sketch, "E19.23.34.0", {"start": v(10.58, -15.84) * mm, "end": v(11, -16.47) * mm});
            skArc(sketch, "E19.26.34.0", {"start": v(9.95, -16.24) * mm, "mid": v(10.27, -16.04) * mm, "end": v(10.58, -15.84) * mm});
            skArc(sketch, "E19.1.35.0", {"start": v(14.49, -12.37) * mm, "mid": v(14.24, -12.65) * mm, "end": v(13.99, -12.93) * mm});
            skLineSegment(sketch, "E19.4.35.0", {"start": v(13.99, -12.93) * mm, "end": v(14.55, -13.45) * mm});
            skArc(sketch, "E19.7.35.0", {"start": v(14.55, -13.45) * mm, "mid": v(14.83, -13.85) * mm, "end": v(14.9, -14.33) * mm});
            skArc(sketch, "E19.11.35.0", {"start": v(14.9, -14.33) * mm, "mid": v(14.77, -14.48) * mm, "end": v(14.62, -14.62) * mm});
            skArc(sketch, "E19.15.35.0", {"start": v(14.33, -14.9) * mm, "mid": v(14.48, -14.77) * mm, "end": v(14.62, -14.62) * mm});
            skArc(sketch, "E19.19.35.0", {"start": v(13.45, -14.55) * mm, "mid": v(13.85, -14.83) * mm, "end": v(14.33, -14.9) * mm});
            skLineSegment(sketch, "E19.23.35.0", {"start": v(12.93, -13.99) * mm, "end": v(13.45, -14.55) * mm});
            skArc(sketch, "E19.26.35.0", {"start": v(12.37, -14.49) * mm, "mid": v(12.65, -14.24) * mm, "end": v(12.93, -13.99) * mm});
            skArc(sketch, "E19.1.36.0", {"start": v(16.24, -9.95) * mm, "mid": v(16.04, -10.27) * mm, "end": v(15.84, -10.58) * mm});
            skLineSegment(sketch, "E19.4.36.0", {"start": v(15.84, -10.58) * mm, "end": v(16.47, -11) * mm});
            skArc(sketch, "E19.7.36.0", {"start": v(16.47, -11) * mm, "mid": v(16.81, -11.36) * mm, "end": v(16.97, -11.83) * mm});
            skArc(sketch, "E19.11.36.0", {"start": v(16.97, -11.83) * mm, "mid": v(16.85, -12) * mm, "end": v(16.73, -12.16) * mm});
            skArc(sketch, "E19.15.36.0", {"start": v(16.5, -12.48) * mm, "mid": v(16.61, -12.32) * mm, "end": v(16.73, -12.16) * mm});
            skArc(sketch, "E19.19.36.0", {"start": v(15.56, -12.27) * mm, "mid": v(16, -12.48) * mm, "end": v(16.5, -12.48) * mm});
            skLineSegment(sketch, "E19.23.36.0", {"start": v(14.96, -11.8) * mm, "end": v(15.56, -12.27) * mm});
            skArc(sketch, "E19.26.36.0", {"start": v(14.49, -12.37) * mm, "mid": v(14.73, -12.09) * mm, "end": v(14.96, -11.8) * mm});
            skArc(sketch, "E19.1.37.0", {"start": v(17.6, -7.3) * mm, "mid": v(17.45, -7.63) * mm, "end": v(17.3, -7.98) * mm});
            skLineSegment(sketch, "E19.4.37.0", {"start": v(17.3, -7.98) * mm, "end": v(18, -8.3) * mm});
            skArc(sketch, "E19.7.37.0", {"start": v(18, -8.3) * mm, "mid": v(18.38, -8.6) * mm, "end": v(18.6, -9.03) * mm});
            skArc(sketch, "E19.11.37.0", {"start": v(18.6, -9.03) * mm, "mid": v(18.52, -9.2) * mm, "end": v(18.43, -9.39) * mm});
            skArc(sketch, "E19.15.37.0", {"start": v(18.24, -9.75) * mm, "mid": v(18.33, -9.57) * mm, "end": v(18.43, -9.39) * mm});
            skArc(sketch, "E19.19.37.0", {"start": v(17.29, -9.68) * mm, "mid": v(17.76, -9.82) * mm, "end": v(18.24, -9.75) * mm});
            skLineSegment(sketch, "E19.23.37.0", {"start": v(16.62, -9.3) * mm, "end": v(17.29, -9.68) * mm});
            skArc(sketch, "E19.26.37.0", {"start": v(16.24, -9.95) * mm, "mid": v(16.44, -9.63) * mm, "end": v(16.62, -9.3) * mm});
            skArc(sketch, "E19.1.38.0", {"start": v(18.52, -4.45) * mm, "mid": v(18.43, -4.8) * mm, "end": v(18.33, -5.17) * mm});
            skLineSegment(sketch, "E19.4.38.0", {"start": v(18.33, -5.17) * mm, "end": v(19.07, -5.38) * mm});
            skArc(sketch, "E19.7.38.0", {"start": v(19.07, -5.38) * mm, "mid": v(19.5, -5.61) * mm, "end": v(19.8, -6) * mm});
            skArc(sketch, "E19.11.38.0", {"start": v(19.8, -6) * mm, "mid": v(19.73, -6.2) * mm, "end": v(19.67, -6.4) * mm});
            skArc(sketch, "E19.15.38.0", {"start": v(19.54, -6.78) * mm, "mid": v(19.6, -6.58) * mm, "end": v(19.67, -6.4) * mm});
            skArc(sketch, "E19.19.38.0", {"start": v(18.59, -6.86) * mm, "mid": v(19.07, -6.92) * mm, "end": v(19.54, -6.78) * mm});
            skLineSegment(sketch, "E19.23.38.0", {"start": v(17.87, -6.6) * mm, "end": v(18.59, -6.86) * mm});
            skArc(sketch, "E19.26.38.0", {"start": v(17.6, -7.3) * mm, "mid": v(17.74, -6.94) * mm, "end": v(17.87, -6.6) * mm});
            skArc(sketch, "E19.1.39.0", {"start": v(19, -1.5) * mm, "mid": v(18.96, -1.87) * mm, "end": v(18.92, -2.24) * mm});
            skLineSegment(sketch, "E19.4.39.0", {"start": v(18.92, -2.24) * mm, "end": v(19.67, -2.33) * mm});
            skArc(sketch, "E19.7.39.0", {"start": v(19.67, -2.33) * mm, "mid": v(20.14, -2.5) * mm, "end": v(20.49, -2.83) * mm});
            skArc(sketch, "E19.11.39.0", {"start": v(20.49, -2.83) * mm, "mid": v(20.46, -3.03) * mm, "end": v(20.43, -3.24) * mm});
            skArc(sketch, "E19.15.39.0", {"start": v(20.36, -3.64) * mm, "mid": v(20.4, -3.44) * mm, "end": v(20.43, -3.24) * mm});
            skArc(sketch, "E19.19.39.0", {"start": v(19.43, -3.87) * mm, "mid": v(19.92, -3.85) * mm, "end": v(20.36, -3.64) * mm});
            skLineSegment(sketch, "E19.23.39.0", {"start": v(18.68, -3.72) * mm, "end": v(19.43, -3.87) * mm});
            skArc(sketch, "E19.26.39.0", {"start": v(18.52, -4.45) * mm, "mid": v(18.6, -4.08) * mm, "end": v(18.68, -3.72) * mm});
            skSolve(sketch);
        }
        {
            var Q0;
            Q0 = qSketchRegion(id + "F0", true);
            extrude(context, id + "F1", {"entities" : qUnion([Q0]), "endBound" : BoundingType.SYMMETRIC, "depth" : 5.74 * mm});
        }
    });
